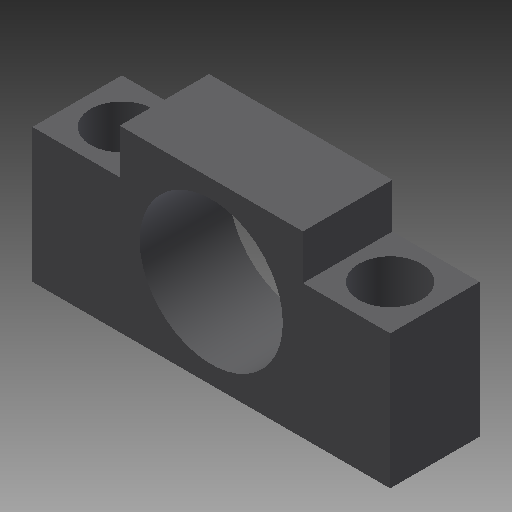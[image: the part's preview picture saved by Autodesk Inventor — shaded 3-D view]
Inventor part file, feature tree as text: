
AUTODESK INVENTOR PART (.ipt)
format: ipt  version: 2018 (Build 220112000, 112)  size: 143,872 bytes
history: native  units: mm
features: other x14, sketch x4, hole x3, extrude x1
ambient origin geometry x8: Origin, YZ Plane, XZ Plane, XY Plane, X Axis, Y Axis, Z Axis, Center Point
bodies: Solid1 (feature_tree)
feature tree (22):
  extrude  "Extrusion1"  TaperAngle=0.0deg  [1 undecoded]
  hole  "Hole1"  [1 undecoded]
  hole  "Hole2"  [1 undecoded]
  hole  "Hole3"  [1 undecoded]
  other  "bf_1_XY"
  other  "bf_1_YZ"
  other  "bf_1_ZX"
  other  "bf_1_X"
  other  "bf_1_Y"
  other  "bf_1_Z"
  other  "bf_1_Center"
  other  "bf_2x_XY"
  other  "bf_2x_YZ"
  other  "bf_2x_ZX"
  other  "bf_2x_Y"
  other  "bf_2x_Z"
  other  "bf_2x_X"
  other  "bf_2x_Center"
  sketch  "Sketch_1"  dims[d0=20.0mm d1=0.0mm]
  sketch  "Sketch2"  dims[d2=9.0mm d3=6.0mm d4=14.0mm d5=11.0mm d6=90.0deg d7=38.0mm d8=0.0mm]
  sketch  "Sketch3"  dims[d9=9.0mm d10=6.0mm d11=14.0mm d12=11.0mm d13=90.0deg d14=38.0mm d15=0.0mm]
  sketch  "Sketch4"  dims[d16=32.0mm d17=6.0mm d18=4.0mm d19=2.0mm d20=90.0deg d21=20.0mm d22=0.0mm d23=0.0mm d24=80.0mm d25=40.0mm d26=10.0mm d27=10.0mm d28=41.0mm d29=20.0mm d30=10.0mm d31=10.0mm]
note: 4 required parameter values undecoded (feature->parameter linkage not recoverable at this tier; creation-order binding heuristic only, values carry confidence <= 0.55)
